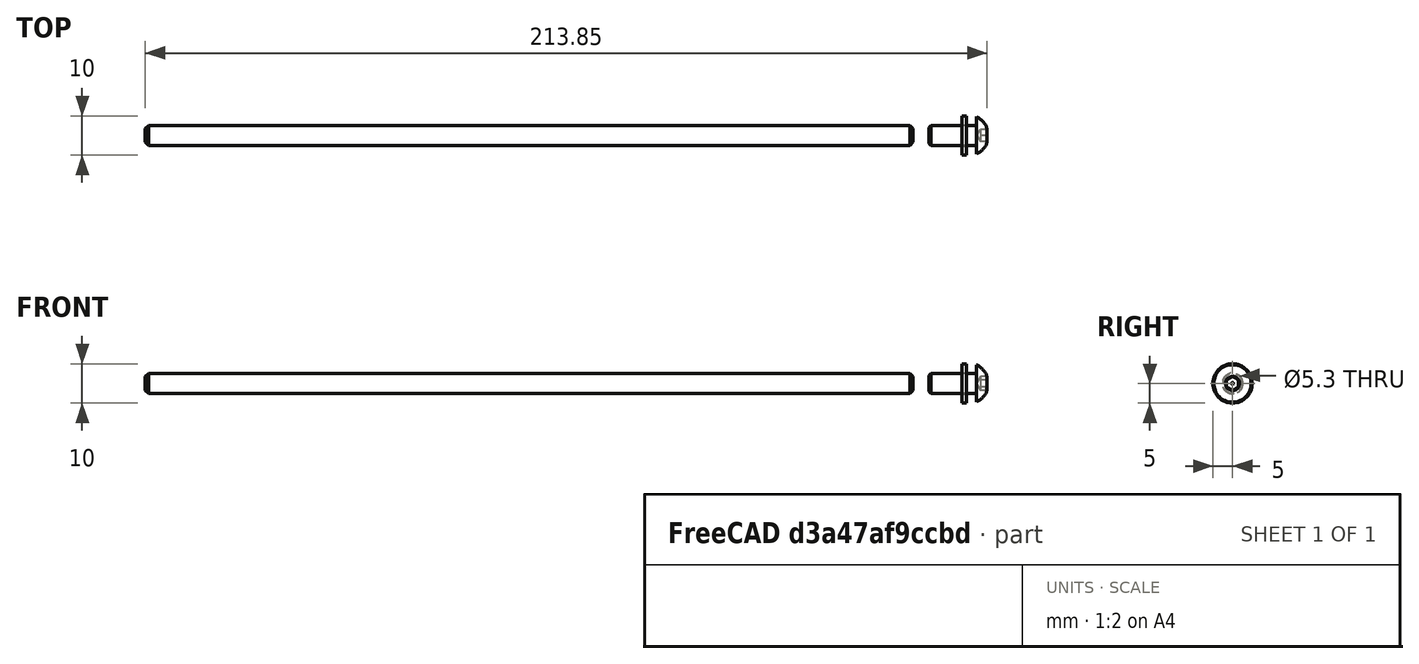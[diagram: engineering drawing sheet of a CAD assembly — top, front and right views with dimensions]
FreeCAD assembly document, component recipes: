
FREECAD ASSEMBLY — COMPONENT RECIPES ("РоликY")

This assembly document has 3 components, labeled P0..P2 below (a component is one placed body or linked part). 0 of them carry a construction recipe — the FreeCAD feature program that regenerates the part from scratch, quoted from this document or its linked companion documents; the rest are supplied as boundary geometry only. No exploded tour is included for this assembly.
COMPONENT P0 — geometry summary ("ШайбаПрав"; no construction recipe available for this part):
  bounding box: 10.0 x 10.0 x 1.1 mm
  tessellated surface: 1,008 triangles
  volume: 62 mm^3 (56% of its bounding box)
  symmetry: revolution-symmetric about the x axis through its bounding-box center; 2-fold rotationally symmetric about the y axis; 2-fold rotationally symmetric about the z axis; mirror-symmetric across its x mid-plane, y mid-plane, z mid-plane
COMPONENT P1 — geometry summary ("DIN6334_2"; no construction recipe available for this part):
  bounding box: 24.0 x 15.0 x 13.0 mm
  tessellated surface: 23,508 triangles
  volume: 2501 mm^3 (53% of its bounding box)
  symmetry: 6-fold rotationally symmetric about the x axis; 2-fold rotationally symmetric about the y axis; 2-fold rotationally symmetric about the z axis
COMPONENT P2 — geometry summary ("ВинтПрав"; no construction recipe available for this part):
  bounding box: 14.8 x 9.5 x 9.5 mm
  tessellated surface: 20,744 triangles
  volume: 340 mm^3 (26% of its bounding box)
  symmetry: revolution-symmetric about the x axis through its bounding-box center; mirror-symmetric across its z mid-plane
PROVENANCE & LICENSES
A FreeCAD (.FCStd) document from a public repository crawl; recipes are the document's own serialized feature recipes (and, for linked parts, companion documents' recipes).
License: as declared in the source repository (recorded in the dataset sidecar).
